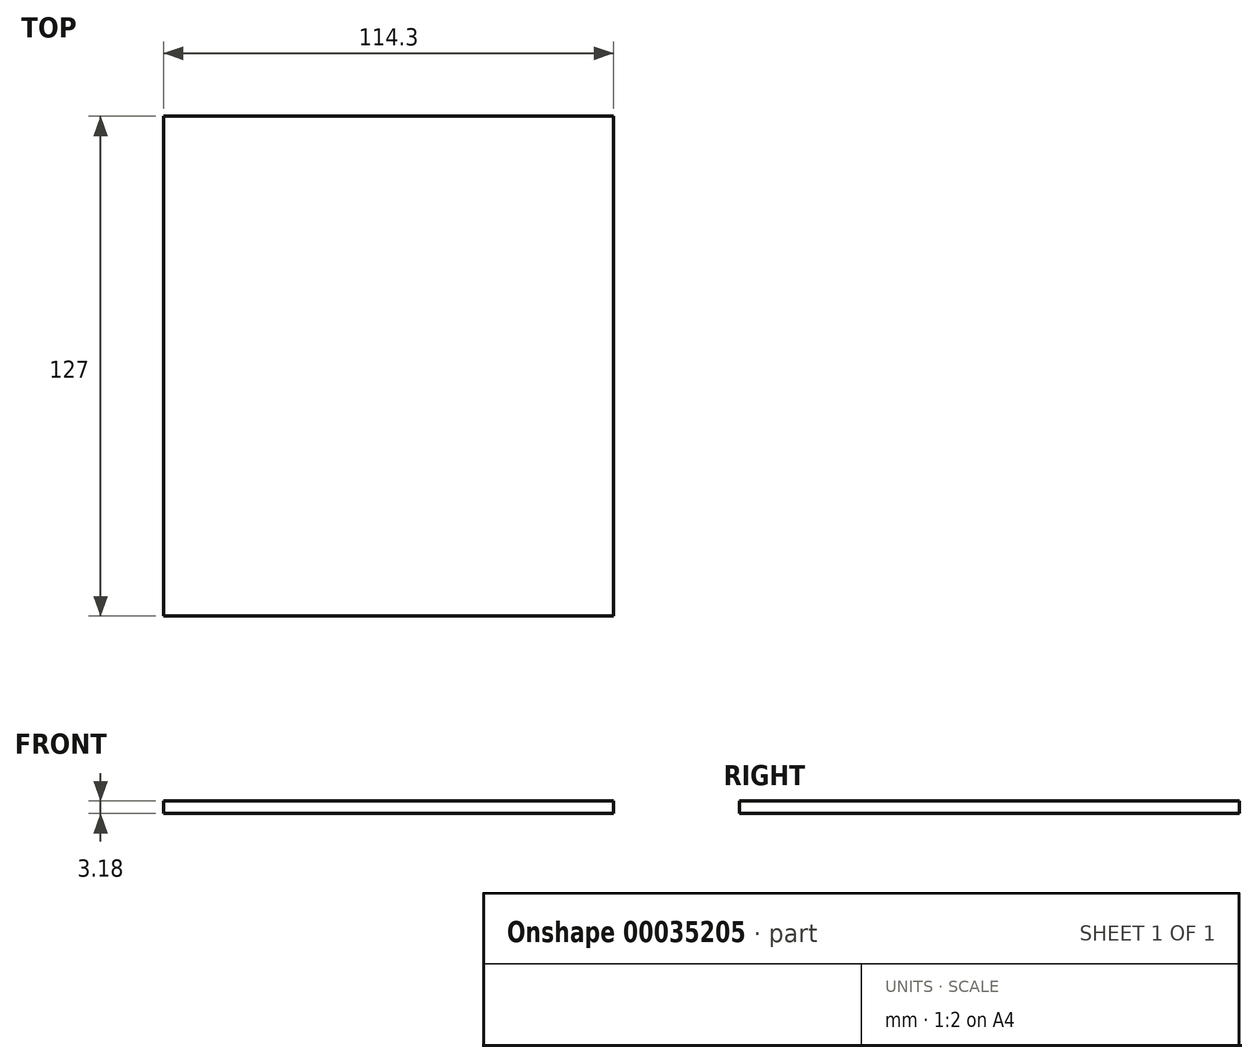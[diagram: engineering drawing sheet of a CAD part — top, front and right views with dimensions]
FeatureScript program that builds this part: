
annotation { "Feature Type Name" : "Feature", "Feature Type Description" : "" }
export const myFeature = defineFeature(function(context is Context, id is Id, definition is map)
    precondition{}
    {
        {
            var Q0;
            Q0=qCreatedBy(makeId("Top.planeOp"),FACE);
            var sketch = newSketch(context, id + "F0", { "sketchPlane" : qUnion([Q0])});
            skLineSegment(sketch, "E0.bottom", {"start": v(-60.1, 85.3) * mm, "end": v(54.2, 85.3) * mm});
            skLineSegment(sketch, "E0.top", {"start": v(-60.1, -41.7) * mm, "end": v(54.2, -41.7) * mm});
            skLineSegment(sketch, "E0.left", {"start": v(-60.1, 85.3) * mm, "end": v(-60.1, -41.7) * mm});
            skLineSegment(sketch, "E0.right", {"start": v(54.2, 85.3) * mm, "end": v(54.2, -41.7) * mm});
            skSolve(sketch);
        }
        {
            var Q0;
            Q0=makeQuery(id+"F0.imprint","IMPRINT",FACE,{"disambiguationData":[TD([[makeQuery(id+"F0.imprint","IMPRINT",EDGE,{"derivedFrom":sQuery(id+"F0.wireOp",EDGE,"E0.bottom")}),-1.0]])]});
            extrude(context, id + "F1", {"entities" : qUnion([Q0]), "depth" : 3.18 * mm});
        }
    });
